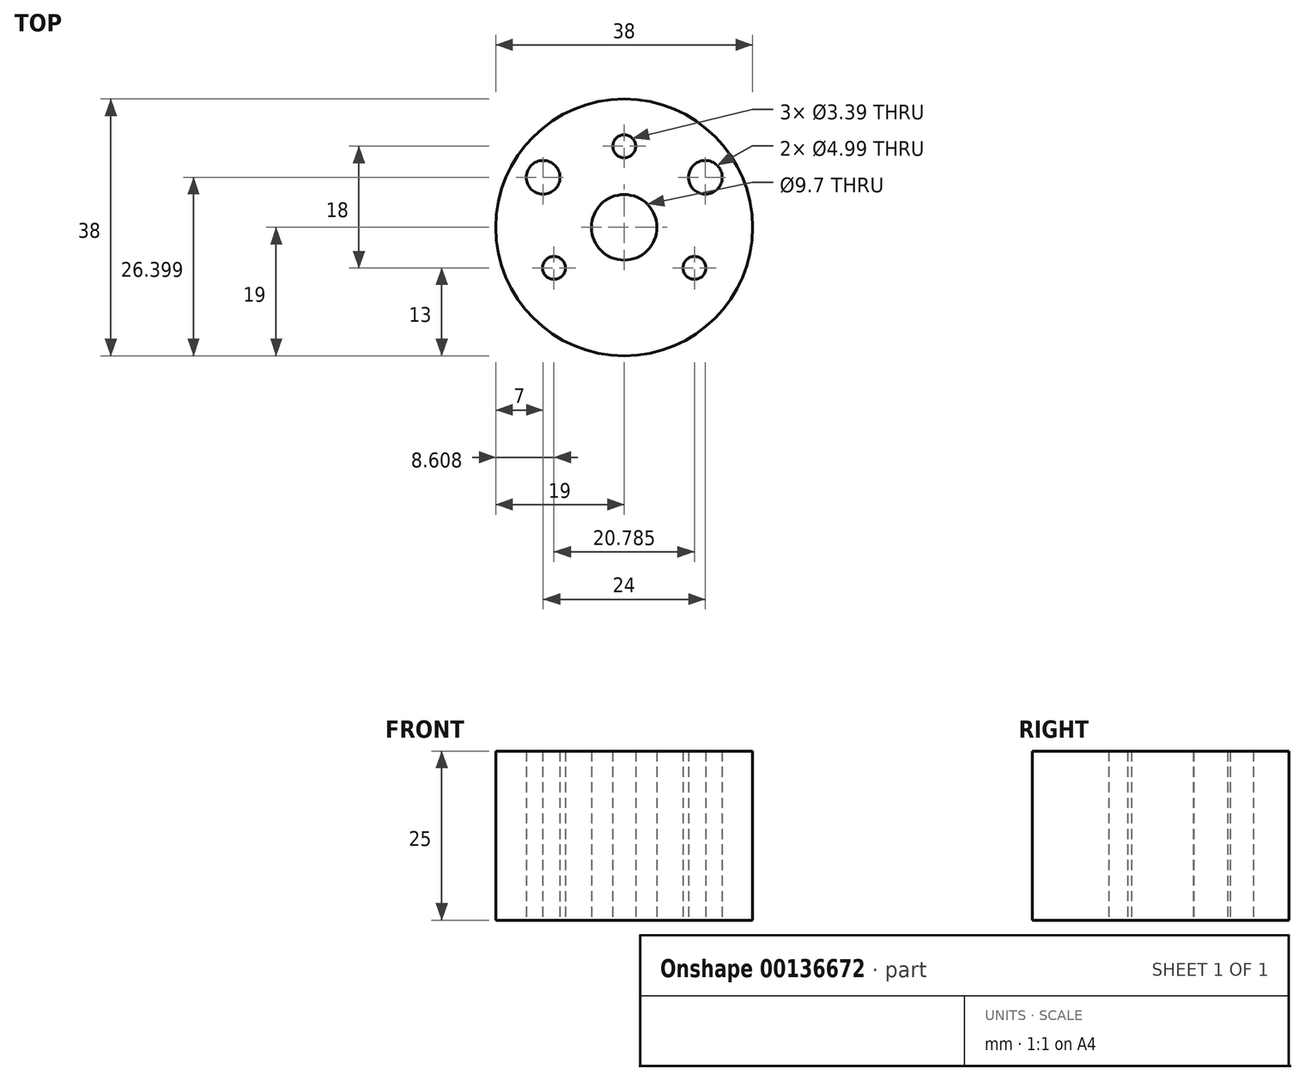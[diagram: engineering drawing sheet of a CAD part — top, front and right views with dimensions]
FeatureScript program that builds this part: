
annotation { "Feature Type Name" : "Feature", "Feature Type Description" : "" }
export const myFeature = defineFeature(function(context is Context, id is Id, definition is map)
    precondition{}
    {
        {
            var Q0;
            Q0=qCreatedBy(makeId("Top.planeOp"),FACE);
            var sketch = newSketch(context, id + "F0", { "sketchPlane" : qUnion([Q0])});
            skCircle(sketch, "E0", {"center": v(0, 0) * mm, "radius": 4.85 * mm});
            skCircle(sketch, "E1", {"center": v(0, 12) * mm, "radius": 1.7 * mm});
            skCircle(sketch, "E2.1.0", {"center": v(-10.4, -6) * mm, "radius": 1.7 * mm});
            skCircle(sketch, "E2.2.0", {"center": v(10.4, -6) * mm, "radius": 1.7 * mm});
            skCircle(sketch, "E3", {"center": v(0, 0) * mm, "radius": 19 * mm});
            skCircle(sketch, "E4", {"center": v(-12, 7.4) * mm, "radius": 2.5 * mm});
            skLineSegment(sketch, "E5", {"start": v(0, 0) * mm, "end": v(0, -13.34) * mm, "construction": true});
            skCircle(sketch, "E6.MirrorC", {"center": v(12, 7.4) * mm, "radius": 2.5 * mm});
            skSolve(sketch);
        }
        {
            var Q0;
            Q0 = qSketchRegion(id + "F0", true);
            extrude(context, id + "F1", {"entities" : qUnion([Q0]), "depth" : 25 * mm});
        }
    });
